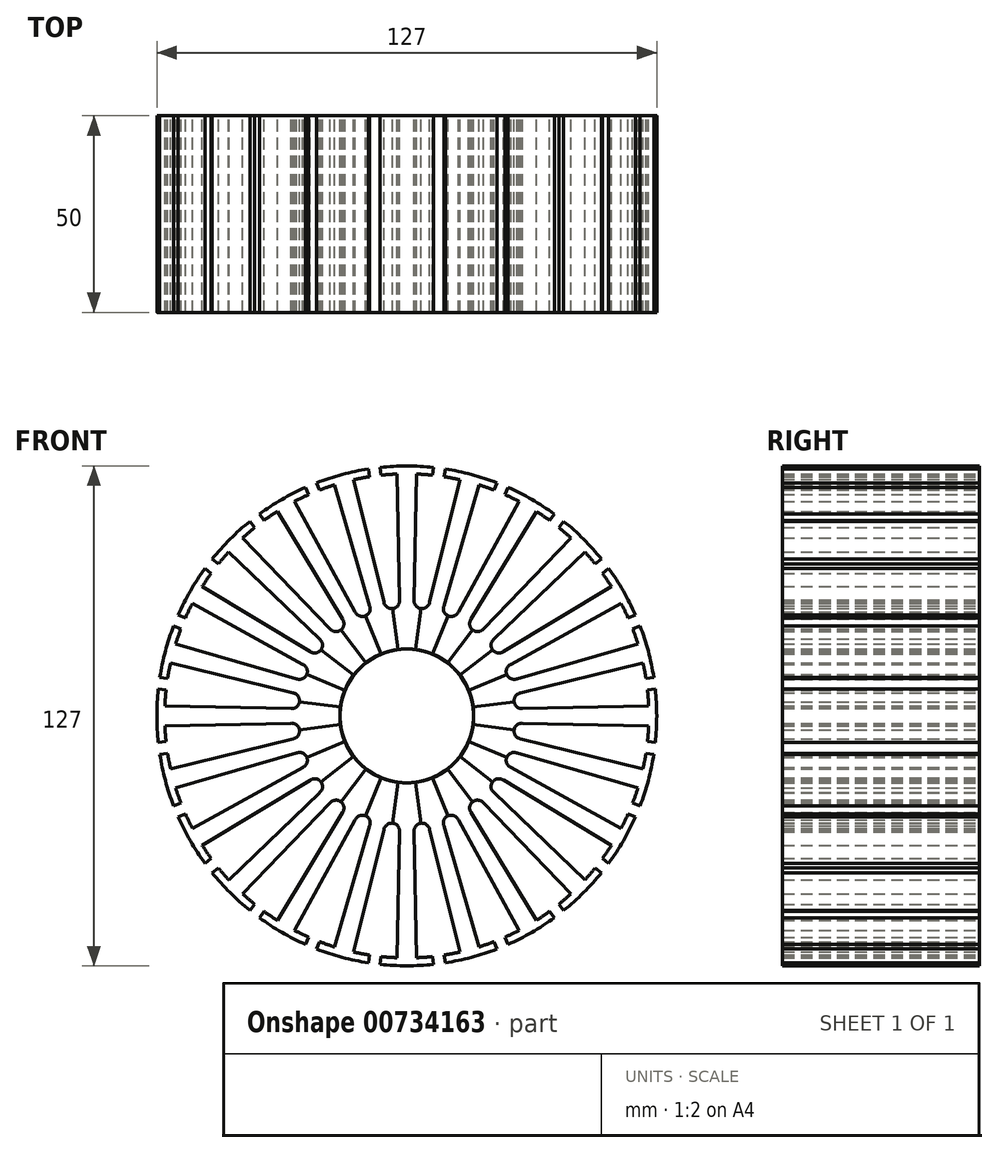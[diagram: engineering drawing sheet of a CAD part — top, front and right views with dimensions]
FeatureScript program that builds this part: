
annotation { "Feature Type Name" : "Feature", "Feature Type Description" : "" }
export const myFeature = defineFeature(function(context is Context, id is Id, definition is map)
    precondition{}
    {
        {
            var Q0;
            Q0=qCreatedBy(makeId("Front.planeOp"),FACE);
            var sketch = newSketch(context, id + "F0", { "sketchPlane" : qUnion([Q0])});
            skCircle(sketch, "E0", {"center": v(0, 0) * mm, "radius": 17 * mm});
            skArc(sketch, "E1", {"start": v(-9.51, 60.76) * mm, "mid": v(-11.5, 60.41) * mm, "end": v(-13.48, 60) * mm});
            skArc(sketch, "E2", {"start": v(1.86, 29.44) * mm, "mid": v(2.28, 28) * mm, "end": v(3.59, 27.26) * mm});
            skArc(sketch, "E3.MirrorC", {"start": v(-1.86, 29.44) * mm, "mid": v(-2.28, 28) * mm, "end": v(-3.59, 27.26) * mm});
            skArc(sketch, "E4.MirrorC", {"start": v(13.1, 26.43) * mm, "mid": v(10.52, 25.4) * mm, "end": v(9.42, 27.96) * mm});
            skArc(sketch, "E5.MirrorC", {"start": v(16.33, 24.57) * mm, "mid": v(16.74, 21.82) * mm, "end": v(19.5, 22.13) * mm});
            skArc(sketch, "E6.MirrorC", {"start": v(24.57, 16.33) * mm, "mid": v(23.1, 15.98) * mm, "end": v(21.82, 16.74) * mm});
            skArc(sketch, "E7.MirrorC", {"start": v(26.43, 13.1) * mm, "mid": v(25.4, 10.52) * mm, "end": v(27.96, 9.42) * mm});
            skArc(sketch, "E8.MirrorC", {"start": v(29.44, 1.86) * mm, "mid": v(27.26, 3.59) * mm, "end": v(28.92, 5.82) * mm});
            skArc(sketch, "E9.MirrorC", {"start": v(29.44, -1.86) * mm, "mid": v(27.26, -3.59) * mm, "end": v(28.92, -5.82) * mm});
            skArc(sketch, "E10.MirrorC", {"start": v(26.43, -13.1) * mm, "mid": v(25.4, -10.52) * mm, "end": v(27.96, -9.42) * mm});
            skArc(sketch, "E11.MirrorC", {"start": v(24.57, -16.33) * mm, "mid": v(21.82, -16.74) * mm, "end": v(22.13, -19.5) * mm});
            skArc(sketch, "E12.MirrorC", {"start": v(16.33, -24.57) * mm, "mid": v(16.74, -21.82) * mm, "end": v(19.5, -22.13) * mm});
            skArc(sketch, "E13.MirrorC", {"start": v(13.1, -26.43) * mm, "mid": v(10.52, -25.4) * mm, "end": v(9.42, -27.96) * mm});
            skArc(sketch, "E14.MirrorC", {"start": v(1.86, -29.44) * mm, "mid": v(3.59, -27.26) * mm, "end": v(5.82, -28.92) * mm});
            skArc(sketch, "E15.MirrorC", {"start": v(-1.86, -29.44) * mm, "mid": v(-3.59, -27.26) * mm, "end": v(-5.82, -28.92) * mm});
            skArc(sketch, "E16.MirrorC", {"start": v(-13.1, -26.43) * mm, "mid": v(-10.52, -25.4) * mm, "end": v(-9.42, -27.96) * mm});
            skArc(sketch, "E17.MirrorC", {"start": v(-16.33, -24.57) * mm, "mid": v(-16.74, -21.82) * mm, "end": v(-19.5, -22.13) * mm});
            skArc(sketch, "E18.MirrorC", {"start": v(-24.57, -16.33) * mm, "mid": v(-21.82, -16.74) * mm, "end": v(-22.13, -19.5) * mm});
            skArc(sketch, "E19.MirrorC", {"start": v(-26.43, -13.1) * mm, "mid": v(-25.4, -10.52) * mm, "end": v(-27.96, -9.42) * mm});
            skArc(sketch, "E20.MirrorC", {"start": v(-29.44, -1.86) * mm, "mid": v(-27.26, -3.59) * mm, "end": v(-28.92, -5.82) * mm});
            skArc(sketch, "E21.MirrorC", {"start": v(-29.44, 1.86) * mm, "mid": v(-27.26, 3.59) * mm, "end": v(-28.92, 5.82) * mm});
            skArc(sketch, "E22.MirrorC", {"start": v(-26.43, 13.1) * mm, "mid": v(-25.4, 10.52) * mm, "end": v(-27.96, 9.42) * mm});
            skArc(sketch, "E23.MirrorC", {"start": v(-24.57, 16.33) * mm, "mid": v(-21.82, 16.74) * mm, "end": v(-22.13, 19.5) * mm});
            skArc(sketch, "E24.MirrorC", {"start": v(-13.1, 26.43) * mm, "mid": v(-10.52, 25.4) * mm, "end": v(-9.42, 27.96) * mm});
            skArc(sketch, "E25.MirrorC", {"start": v(-16.33, 24.57) * mm, "mid": v(-16.74, 21.82) * mm, "end": v(-19.5, 22.13) * mm});
            skLineSegment(sketch, "E26", {"start": v(-2.5, 61.45) * mm, "end": v(-1.86, 29.44) * mm});
            skLineSegment(sketch, "E27", {"start": v(2.5, 61.45) * mm, "end": v(1.85, 29.44) * mm});
            skLineSegment(sketch, "E28.MirrorCS", {"start": v(13.49, 60) * mm, "end": v(5.83, 28.92) * mm});
            skLineSegment(sketch, "E29.MirrorCS", {"start": v(-13.48, 60) * mm, "end": v(-5.82, 28.92) * mm});
            skLineSegment(sketch, "E30.MirrorCS", {"start": v(18.32, 58.7) * mm, "end": v(9.41, 27.96) * mm});
            skLineSegment(sketch, "E31.MirrorCS", {"start": v(28.56, 54.47) * mm, "end": v(13.12, 26.42) * mm});
            skLineSegment(sketch, "E32.MirrorCS", {"start": v(32.9, 51.96) * mm, "end": v(16.33, 24.57) * mm});
            skLineSegment(sketch, "E33.MirrorCS", {"start": v(41.68, 45.22) * mm, "end": v(19.5, 22.13) * mm});
            skLineSegment(sketch, "E34.MirrorCS", {"start": v(45.22, 41.68) * mm, "end": v(22.13, 19.5) * mm});
            skLineSegment(sketch, "E35.MirrorCS", {"start": v(54.47, 28.56) * mm, "end": v(26.42, 13.12) * mm});
            skLineSegment(sketch, "E36.MirrorCS", {"start": v(58.7, 18.32) * mm, "end": v(27.96, 9.41) * mm});
            skLineSegment(sketch, "E37.MirrorCS", {"start": v(60, 13.49) * mm, "end": v(28.92, 5.83) * mm});
            skLineSegment(sketch, "E38.MirrorCS", {"start": v(61.45, 2.5) * mm, "end": v(29.44, 1.85) * mm});
            skLineSegment(sketch, "E39.MirrorCS", {"start": v(61.45, -2.5) * mm, "end": v(29.44, -1.86) * mm});
            skLineSegment(sketch, "E40.MirrorCS", {"start": v(60, -13.48) * mm, "end": v(28.92, -5.82) * mm});
            skLineSegment(sketch, "E41.MirrorCS", {"start": v(58.7, -18.33) * mm, "end": v(27.96, -9.42) * mm});
            skLineSegment(sketch, "E42.MirrorCS", {"start": v(54.47, -28.55) * mm, "end": v(26.43, -13.1) * mm});
            skLineSegment(sketch, "E43.MirrorCS", {"start": v(51.97, -32.89) * mm, "end": v(24.57, -16.33) * mm});
            skLineSegment(sketch, "E44.MirrorCS", {"start": v(45.22, -41.68) * mm, "end": v(22.13, -19.5) * mm});
            skLineSegment(sketch, "E45.MirrorCS", {"start": v(41.68, -45.22) * mm, "end": v(19.5, -22.13) * mm});
            skLineSegment(sketch, "E46.MirrorCS", {"start": v(32.89, -51.97) * mm, "end": v(16.33, -24.57) * mm});
            skLineSegment(sketch, "E47.MirrorCS", {"start": v(51.96, 32.9) * mm, "end": v(24.57, 16.33) * mm});
            skLineSegment(sketch, "E48.MirrorCS", {"start": v(28.56, -54.47) * mm, "end": v(13.12, -26.42) * mm});
            skLineSegment(sketch, "E49.MirrorCS", {"start": v(18.32, -58.7) * mm, "end": v(9.41, -27.96) * mm});
            skLineSegment(sketch, "E50.MirrorCS", {"start": v(13.49, -60) * mm, "end": v(5.83, -28.92) * mm});
            skLineSegment(sketch, "E51.MirrorCS", {"start": v(2.5, -61.45) * mm, "end": v(1.85, -29.44) * mm});
            skLineSegment(sketch, "E52.MirrorCS", {"start": v(-2.5, -61.45) * mm, "end": v(-1.85, -29.44) * mm});
            skLineSegment(sketch, "E53.MirrorCS", {"start": v(-13.49, -60) * mm, "end": v(-5.83, -28.92) * mm});
            skLineSegment(sketch, "E54.MirrorCS", {"start": v(-18.32, -58.7) * mm, "end": v(-9.41, -27.96) * mm});
            skLineSegment(sketch, "E55.MirrorCS", {"start": v(-28.56, -54.47) * mm, "end": v(-13.12, -26.42) * mm});
            skLineSegment(sketch, "E56.MirrorCS", {"start": v(-32.89, -51.97) * mm, "end": v(-16.33, -24.57) * mm});
            skLineSegment(sketch, "E57.MirrorCS", {"start": v(-41.68, -45.22) * mm, "end": v(-19.5, -22.13) * mm});
            skLineSegment(sketch, "E58.MirrorCS", {"start": v(-45.22, -41.68) * mm, "end": v(-22.13, -19.5) * mm});
            skLineSegment(sketch, "E59.MirrorCS", {"start": v(-51.97, -32.89) * mm, "end": v(-24.57, -16.33) * mm});
            skLineSegment(sketch, "E60.MirrorCS", {"start": v(-54.47, -28.56) * mm, "end": v(-26.42, -13.12) * mm});
            skLineSegment(sketch, "E61.MirrorCS", {"start": v(-58.7, -18.32) * mm, "end": v(-27.96, -9.41) * mm});
            skLineSegment(sketch, "E62.MirrorCS", {"start": v(-60, -13.49) * mm, "end": v(-28.92, -5.83) * mm});
            skLineSegment(sketch, "E63.MirrorCS", {"start": v(-61.45, -2.5) * mm, "end": v(-29.44, -1.85) * mm});
            skLineSegment(sketch, "E64.MirrorCS", {"start": v(-61.45, 2.5) * mm, "end": v(-29.44, 1.85) * mm});
            skLineSegment(sketch, "E65.MirrorCS", {"start": v(-60, 13.49) * mm, "end": v(-28.92, 5.83) * mm});
            skLineSegment(sketch, "E66.MirrorCS", {"start": v(-58.7, 18.32) * mm, "end": v(-27.96, 9.41) * mm});
            skLineSegment(sketch, "E67.MirrorCS", {"start": v(-54.47, 28.56) * mm, "end": v(-26.42, 13.12) * mm});
            skLineSegment(sketch, "E68.MirrorCS", {"start": v(-51.97, 32.89) * mm, "end": v(-24.57, 16.33) * mm});
            skLineSegment(sketch, "E69.MirrorCS", {"start": v(-45.22, 41.68) * mm, "end": v(-22.13, 19.5) * mm});
            skLineSegment(sketch, "E70.MirrorCS", {"start": v(-41.68, 45.22) * mm, "end": v(-19.5, 22.13) * mm});
            skLineSegment(sketch, "E71.MirrorCS", {"start": v(-32.89, 51.97) * mm, "end": v(-16.33, 24.57) * mm});
            skLineSegment(sketch, "E72.MirrorCS", {"start": v(-28.56, 54.47) * mm, "end": v(-13.12, 26.42) * mm});
            skLineSegment(sketch, "E73.MirrorCS", {"start": v(-18.32, 58.7) * mm, "end": v(-9.41, 27.96) * mm});
            skArc(sketch, "E74.MirrorCS", {"start": v(22.13, 19.5) * mm, "mid": v(21.42, 18.19) * mm, "end": v(21.82, 16.74) * mm});
            skLineSegment(sketch, "E75.MirrorCS", {"start": v(-6.8, 63.13) * mm, "end": v(-6.54, 61.15) * mm});
            skLineSegment(sketch, "E76.MirrorCS", {"start": v(-9.77, 62.74) * mm, "end": v(-9.51, 60.76) * mm});
            skLineSegment(sketch, "E77.MirrorCS", {"start": v(-22.9, 59.22) * mm, "end": v(-22.14, 57.38) * mm});
            skLineSegment(sketch, "E78.MirrorCS", {"start": v(-25.69, 58.1) * mm, "end": v(-24.91, 56.23) * mm});
            skLineSegment(sketch, "E79.MirrorCS", {"start": v(-37.47, 51.3) * mm, "end": v(-36.24, 49.69) * mm});
            skLineSegment(sketch, "E80.MirrorCS", {"start": v(-39.84, 49.45) * mm, "end": v(-38.62, 47.86) * mm});
            skLineSegment(sketch, "E81.MirrorCS", {"start": v(-49.45, 39.84) * mm, "end": v(-47.86, 38.62) * mm});
            skLineSegment(sketch, "E82.MirrorCS", {"start": v(-51.3, 37.47) * mm, "end": v(-49.69, 36.24) * mm});
            skLineSegment(sketch, "E83.MirrorCS", {"start": v(-59.22, 22.9) * mm, "end": v(-57.38, 22.14) * mm});
            skLineSegment(sketch, "E84.MirrorCS", {"start": v(-58.1, 25.69) * mm, "end": v(-56.23, 24.91) * mm});
            skLineSegment(sketch, "E85.MirrorCS", {"start": v(-62.74, 9.77) * mm, "end": v(-60.76, 9.51) * mm});
            skLineSegment(sketch, "E86.MirrorCS", {"start": v(-63.15, 6.8) * mm, "end": v(-61.15, 6.54) * mm});
            skLineSegment(sketch, "E87.MirrorCS", {"start": v(-63.15, -6.8) * mm, "end": v(-61.15, -6.54) * mm});
            skLineSegment(sketch, "E88.MirrorCS", {"start": v(-62.74, -9.77) * mm, "end": v(-60.76, -9.51) * mm});
            skLineSegment(sketch, "E89.MirrorCS", {"start": v(-59.22, -22.9) * mm, "end": v(-57.38, -22.14) * mm});
            skLineSegment(sketch, "E90.MirrorCS", {"start": v(-58.1, -25.69) * mm, "end": v(-56.23, -24.91) * mm});
            skLineSegment(sketch, "E91.MirrorCS", {"start": v(-51.3, -37.47) * mm, "end": v(-49.69, -36.24) * mm});
            skLineSegment(sketch, "E92.MirrorCS", {"start": v(-49.45, -39.84) * mm, "end": v(-47.86, -38.62) * mm});
            skLineSegment(sketch, "E93.MirrorCS", {"start": v(-39.84, -49.45) * mm, "end": v(-38.62, -47.86) * mm});
            skLineSegment(sketch, "E94.MirrorCS", {"start": v(-37.47, -51.3) * mm, "end": v(-36.24, -49.69) * mm});
            skLineSegment(sketch, "E95.MirrorCS", {"start": v(-25.69, -58.1) * mm, "end": v(-24.91, -56.23) * mm});
            skLineSegment(sketch, "E96.MirrorCS", {"start": v(-22.9, -59.22) * mm, "end": v(-22.14, -57.38) * mm});
            skLineSegment(sketch, "E97.MirrorCS", {"start": v(-9.77, -62.74) * mm, "end": v(-9.51, -60.76) * mm});
            skLineSegment(sketch, "E98.MirrorCS", {"start": v(-6.8, -63.15) * mm, "end": v(-6.54, -61.15) * mm});
            skLineSegment(sketch, "E99.MirrorCS", {"start": v(6.8, -63.15) * mm, "end": v(6.54, -61.15) * mm});
            skLineSegment(sketch, "E100.MirrorCS", {"start": v(9.77, -62.74) * mm, "end": v(9.51, -60.76) * mm});
            skLineSegment(sketch, "E101.MirrorCS", {"start": v(22.9, -59.22) * mm, "end": v(22.14, -57.38) * mm});
            skLineSegment(sketch, "E102.MirrorCS", {"start": v(25.69, -58.1) * mm, "end": v(24.91, -56.23) * mm});
            skLineSegment(sketch, "E103.MirrorCS", {"start": v(37.47, -51.3) * mm, "end": v(36.24, -49.69) * mm});
            skLineSegment(sketch, "E104.MirrorCS", {"start": v(39.84, -49.45) * mm, "end": v(38.62, -47.86) * mm});
            skLineSegment(sketch, "E105.MirrorCS", {"start": v(49.45, -39.84) * mm, "end": v(47.86, -38.62) * mm});
            skLineSegment(sketch, "E106.MirrorCS", {"start": v(51.3, -37.47) * mm, "end": v(49.69, -36.24) * mm});
            skLineSegment(sketch, "E107.MirrorCS", {"start": v(58.1, -25.69) * mm, "end": v(56.23, -24.91) * mm});
            skLineSegment(sketch, "E108.MirrorCS", {"start": v(59.22, -22.9) * mm, "end": v(57.38, -22.14) * mm});
            skLineSegment(sketch, "E109.MirrorCS", {"start": v(63.15, -6.8) * mm, "end": v(61.15, -6.54) * mm});
            skLineSegment(sketch, "E110.MirrorCS", {"start": v(62.74, -9.77) * mm, "end": v(60.76, -9.51) * mm});
            skLineSegment(sketch, "E111.MirrorCS", {"start": v(63.15, 6.8) * mm, "end": v(61.15, 6.54) * mm});
            skLineSegment(sketch, "E112.MirrorCS", {"start": v(62.74, 9.77) * mm, "end": v(60.76, 9.51) * mm});
            skLineSegment(sketch, "E113.MirrorCS", {"start": v(59.22, 22.9) * mm, "end": v(57.38, 22.14) * mm});
            skLineSegment(sketch, "E114.MirrorCS", {"start": v(58.1, 25.69) * mm, "end": v(56.23, 24.91) * mm});
            skLineSegment(sketch, "E115.MirrorCS", {"start": v(51.3, 37.47) * mm, "end": v(49.69, 36.24) * mm});
            skLineSegment(sketch, "E116.MirrorCS", {"start": v(49.45, 39.84) * mm, "end": v(47.86, 38.62) * mm});
            skLineSegment(sketch, "E117.MirrorCS", {"start": v(39.84, 49.45) * mm, "end": v(38.62, 47.86) * mm});
            skLineSegment(sketch, "E118.MirrorCS", {"start": v(37.47, 51.3) * mm, "end": v(36.24, 49.69) * mm});
            skLineSegment(sketch, "E119.MirrorCS", {"start": v(6.8, 63.13) * mm, "end": v(6.54, 61.15) * mm});
            skLineSegment(sketch, "E120.MirrorCS", {"start": v(9.77, 62.74) * mm, "end": v(9.51, 60.76) * mm});
            skLineSegment(sketch, "E121.MirrorCS", {"start": v(22.9, 59.22) * mm, "end": v(22.14, 57.38) * mm});
            skLineSegment(sketch, "E122.MirrorCS", {"start": v(25.69, 58.1) * mm, "end": v(24.91, 56.23) * mm});
            skArc(sketch, "E123.trimOffspring", {"start": v(-24.91, 56.23) * mm, "mid": v(-26.75, 55.38) * mm, "end": v(-28.56, 54.47) * mm});
            skArc(sketch, "E124.trimOffspring", {"start": v(-25.68, 58.08) * mm, "mid": v(-31.75, 55) * mm, "end": v(-37.46, 51.28) * mm});
            skArc(sketch, "E125.trimOffspring", {"start": v(-38.62, 47.86) * mm, "mid": v(-40.17, 46.57) * mm, "end": v(-41.68, 45.22) * mm});
            skArc(sketch, "E126.trimOffspring", {"start": v(-39.84, 49.45) * mm, "mid": v(-44.9, 44.9) * mm, "end": v(-49.45, 39.84) * mm});
            skArc(sketch, "E127.trimOffspring", {"start": v(-57.38, 22.14) * mm, "mid": v(-58.07, 20.24) * mm, "end": v(-58.7, 18.32) * mm});
            skArc(sketch, "E128.trimOffspring", {"start": v(-59.22, 22.9) * mm, "mid": v(-61.34, 16.44) * mm, "end": v(-62.74, 9.77) * mm});
            skArc(sketch, "E129.trimOffspring", {"start": v(-51.28, 37.46) * mm, "mid": v(-55, 31.75) * mm, "end": v(-58.08, 25.68) * mm});
            skArc(sketch, "E130.trimOffspring", {"start": v(-49.69, 36.24) * mm, "mid": v(-50.86, 34.58) * mm, "end": v(-51.97, 32.89) * mm});
            skArc(sketch, "E131.trimOffspring", {"start": v(-61.15, 6.54) * mm, "mid": v(-61.33, 4.52) * mm, "end": v(-61.45, 2.5) * mm});
            skArc(sketch, "E132.trimOffspring", {"start": v(-63.13, 6.8) * mm, "mid": v(-63.5, 0) * mm, "end": v(-63.13, -6.8) * mm});
            skArc(sketch, "E133.trimOffspring", {"start": v(-60.76, -9.51) * mm, "mid": v(-60.41, -11.5) * mm, "end": v(-60, -13.49) * mm});
            skArc(sketch, "E134.trimOffspring", {"start": v(-56.23, -24.91) * mm, "mid": v(-55.38, -26.75) * mm, "end": v(-54.47, -28.56) * mm});
            skArc(sketch, "E135.trimOffspring", {"start": v(-62.74, -9.77) * mm, "mid": v(-61.34, -16.44) * mm, "end": v(-59.22, -22.9) * mm});
            skArc(sketch, "E136.trimOffspring", {"start": v(-58.08, -25.68) * mm, "mid": v(-55, -31.75) * mm, "end": v(-51.28, -37.46) * mm});
            skArc(sketch, "E137.trimOffspring", {"start": v(-49.45, -39.84) * mm, "mid": v(-44.9, -44.9) * mm, "end": v(-39.84, -49.45) * mm});
            skArc(sketch, "E138.trimOffspring", {"start": v(-47.86, -38.62) * mm, "mid": v(-46.57, -40.17) * mm, "end": v(-45.22, -41.68) * mm});
            skArc(sketch, "E139.trimOffspring", {"start": v(-37.46, -51.28) * mm, "mid": v(-31.75, -55) * mm, "end": v(-25.68, -58.08) * mm});
            skArc(sketch, "E140.trimOffspring", {"start": v(-36.24, -49.69) * mm, "mid": v(-34.58, -50.86) * mm, "end": v(-32.89, -51.97) * mm});
            skArc(sketch, "E141.trimOffspring", {"start": v(-22.14, -57.38) * mm, "mid": v(-20.24, -58.07) * mm, "end": v(-18.32, -58.7) * mm});
            skArc(sketch, "E142.trimOffspring", {"start": v(-22.9, -59.22) * mm, "mid": v(-16.44, -61.34) * mm, "end": v(-9.77, -62.74) * mm});
            skArc(sketch, "E143.trimOffspring", {"start": v(-6.54, -61.15) * mm, "mid": v(-4.52, -61.33) * mm, "end": v(-2.5, -61.45) * mm});
            skArc(sketch, "E144.trimOffspring", {"start": v(-6.8, -63.13) * mm, "mid": v(0, -63.5) * mm, "end": v(6.8, -63.13) * mm});
            skArc(sketch, "E145.trimOffspring", {"start": v(9.51, -60.76) * mm, "mid": v(11.5, -60.41) * mm, "end": v(13.49, -60) * mm});
            skArc(sketch, "E146.trimOffspring", {"start": v(9.77, -62.74) * mm, "mid": v(16.44, -61.34) * mm, "end": v(22.9, -59.22) * mm});
            skArc(sketch, "E147.trimOffspring", {"start": v(24.91, -56.23) * mm, "mid": v(26.75, -55.38) * mm, "end": v(28.56, -54.47) * mm});
            skArc(sketch, "E148.trimOffspring", {"start": v(25.68, -58.08) * mm, "mid": v(31.75, -55) * mm, "end": v(37.46, -51.28) * mm});
            skArc(sketch, "E149.trimOffspring", {"start": v(38.62, -47.86) * mm, "mid": v(40.17, -46.57) * mm, "end": v(41.68, -45.22) * mm});
            skArc(sketch, "E150.trimOffspring", {"start": v(39.84, -49.45) * mm, "mid": v(44.9, -44.9) * mm, "end": v(49.45, -39.84) * mm});
            skArc(sketch, "E151.trimOffspring", {"start": v(49.69, -36.24) * mm, "mid": v(50.86, -34.58) * mm, "end": v(51.97, -32.89) * mm});
            skArc(sketch, "E152.trimOffspring", {"start": v(51.28, -37.46) * mm, "mid": v(55, -31.75) * mm, "end": v(58.08, -25.68) * mm});
            skArc(sketch, "E153.trimOffspring", {"start": v(57.38, -22.14) * mm, "mid": v(58.07, -20.24) * mm, "end": v(58.7, -18.33) * mm});
            skArc(sketch, "E154.trimOffspring", {"start": v(59.22, -22.9) * mm, "mid": v(61.34, -16.44) * mm, "end": v(62.74, -9.77) * mm});
            skArc(sketch, "E155.trimOffspring", {"start": v(61.15, -6.54) * mm, "mid": v(61.33, -4.52) * mm, "end": v(61.45, -2.5) * mm});
            skArc(sketch, "E156.trimOffspring", {"start": v(63.13, -6.8) * mm, "mid": v(63.5, 0) * mm, "end": v(63.13, 6.8) * mm});
            skArc(sketch, "E157.trimOffspring", {"start": v(60.76, 9.51) * mm, "mid": v(60.41, 11.5) * mm, "end": v(60, 13.49) * mm});
            skArc(sketch, "E158.trimOffspring", {"start": v(56.23, 24.91) * mm, "mid": v(55.38, 26.75) * mm, "end": v(54.47, 28.56) * mm});
            skArc(sketch, "E159.trimOffspring", {"start": v(58.08, 25.68) * mm, "mid": v(55, 31.75) * mm, "end": v(51.28, 37.46) * mm});
            skArc(sketch, "E160.trimOffspring", {"start": v(47.86, 38.62) * mm, "mid": v(46.57, 40.17) * mm, "end": v(45.22, 41.68) * mm});
            skArc(sketch, "E161.trimOffspring", {"start": v(49.45, 39.84) * mm, "mid": v(44.9, 44.9) * mm, "end": v(39.84, 49.45) * mm});
            skArc(sketch, "E162.trimOffspring", {"start": v(36.24, 49.69) * mm, "mid": v(34.59, 50.85) * mm, "end": v(32.9, 51.96) * mm});
            skArc(sketch, "E163.trimOffspring", {"start": v(37.46, 51.28) * mm, "mid": v(31.75, 55) * mm, "end": v(25.68, 58.08) * mm});
            skArc(sketch, "E164.trimOffspring", {"start": v(22.14, 57.38) * mm, "mid": v(20.24, 58.07) * mm, "end": v(18.32, 58.7) * mm});
            skArc(sketch, "E165.trimOffspring", {"start": v(22.9, 59.22) * mm, "mid": v(16.44, 61.34) * mm, "end": v(9.77, 62.74) * mm});
            skArc(sketch, "E166.trimOffspring", {"start": v(6.8, 63.13) * mm, "mid": v(0, 63.5) * mm, "end": v(-6.8, 63.13) * mm});
            skArc(sketch, "E167.trimOffspring", {"start": v(6.54, 61.15) * mm, "mid": v(4.52, 61.33) * mm, "end": v(2.5, 61.45) * mm});
            skArc(sketch, "E168", {"start": v(-22.9, 59.22) * mm, "mid": v(-16.44, 61.34) * mm, "end": v(-9.77, 62.74) * mm});
            skArc(sketch, "E169.trimOffspring", {"start": v(-45.22, 41.68) * mm, "mid": v(-46.57, 40.17) * mm, "end": v(-47.86, 38.62) * mm});
            skArc(sketch, "E170.trimOffspring", {"start": v(-32.89, 51.97) * mm, "mid": v(-34.58, 50.86) * mm, "end": v(-36.24, 49.69) * mm});
            skArc(sketch, "E171.trimOffspring", {"start": v(-54.47, 28.56) * mm, "mid": v(-55.38, 26.75) * mm, "end": v(-56.23, 24.91) * mm});
            skArc(sketch, "E172.trimOffspring", {"start": v(-60, 13.49) * mm, "mid": v(-60.41, 11.5) * mm, "end": v(-60.76, 9.51) * mm});
            skArc(sketch, "E173.trimOffspring", {"start": v(-58.7, -18.32) * mm, "mid": v(-58.07, -20.24) * mm, "end": v(-57.38, -22.14) * mm});
            skArc(sketch, "E174.trimOffspring", {"start": v(-51.97, -32.89) * mm, "mid": v(-50.86, -34.58) * mm, "end": v(-49.69, -36.24) * mm});
            skArc(sketch, "E175.trimOffspring", {"start": v(-61.45, -2.5) * mm, "mid": v(-61.33, -4.52) * mm, "end": v(-61.15, -6.54) * mm});
            skArc(sketch, "E176.trimOffspring", {"start": v(-41.68, -45.22) * mm, "mid": v(-40.17, -46.57) * mm, "end": v(-38.62, -47.86) * mm});
            skArc(sketch, "E177.trimOffspring", {"start": v(-28.56, -54.47) * mm, "mid": v(-26.75, -55.38) * mm, "end": v(-24.91, -56.23) * mm});
            skArc(sketch, "E178.trimOffspring", {"start": v(-13.49, -60) * mm, "mid": v(-11.5, -60.41) * mm, "end": v(-9.51, -60.76) * mm});
            skArc(sketch, "E179.trimOffspring", {"start": v(2.5, -61.45) * mm, "mid": v(4.52, -61.33) * mm, "end": v(6.54, -61.15) * mm});
            skArc(sketch, "E180.trimOffspring", {"start": v(18.32, -58.7) * mm, "mid": v(20.24, -58.07) * mm, "end": v(22.14, -57.38) * mm});
            skArc(sketch, "E181.trimOffspring", {"start": v(32.89, -51.97) * mm, "mid": v(34.58, -50.86) * mm, "end": v(36.24, -49.69) * mm});
            skArc(sketch, "E182.trimOffspring", {"start": v(45.22, -41.68) * mm, "mid": v(46.57, -40.17) * mm, "end": v(47.86, -38.62) * mm});
            skArc(sketch, "E183.trimOffspring", {"start": v(54.47, -28.55) * mm, "mid": v(55.38, -26.75) * mm, "end": v(56.23, -24.91) * mm});
            skArc(sketch, "E184.trimOffspring", {"start": v(60, -13.48) * mm, "mid": v(60.41, -11.5) * mm, "end": v(60.76, -9.51) * mm});
            skArc(sketch, "E185.trimOffspring", {"start": v(61.45, 2.5) * mm, "mid": v(61.33, 4.52) * mm, "end": v(61.15, 6.54) * mm});
            skArc(sketch, "E186.trimOffspring", {"start": v(58.7, 18.32) * mm, "mid": v(58.07, 20.24) * mm, "end": v(57.38, 22.14) * mm});
            skArc(sketch, "E187.trimOffspring", {"start": v(51.96, 32.9) * mm, "mid": v(50.85, 34.59) * mm, "end": v(49.69, 36.24) * mm});
            skArc(sketch, "E188.trimOffspring", {"start": v(41.68, 45.22) * mm, "mid": v(40.17, 46.57) * mm, "end": v(38.62, 47.86) * mm});
            skArc(sketch, "E189.trimOffspring", {"start": v(28.56, 54.47) * mm, "mid": v(26.75, 55.38) * mm, "end": v(24.91, 56.23) * mm});
            skArc(sketch, "E190.trimOffspring", {"start": v(13.49, 60) * mm, "mid": v(11.5, 60.41) * mm, "end": v(9.51, 60.76) * mm});
            skArc(sketch, "E191.trimOffspring", {"start": v(-2.5, 61.45) * mm, "mid": v(-4.52, 61.33) * mm, "end": v(-6.54, 61.15) * mm});
            skArc(sketch, "E192.trimOffspring", {"start": v(-18.32, 58.7) * mm, "mid": v(-20.24, 58.07) * mm, "end": v(-22.14, 57.38) * mm});
            skArc(sketch, "E193", {"start": v(59.22, 22.9) * mm, "mid": v(61.34, 16.44) * mm, "end": v(62.74, 9.77) * mm});
            skLineSegment(sketch, "E194", {"start": v(3.59, 27.26) * mm, "end": v(0, 0) * mm});
            skLineSegment(sketch, "E195", {"start": v(-3.59, 27.26) * mm, "end": v(0, 0) * mm});
            skLineSegment(sketch, "E196", {"start": v(1.85, 29.44) * mm, "end": v(1.86, 29.44) * mm});
            skSolve(sketch);
        }
        {
            var Q0;
            Q0 = qSketchRegion(id + "F0", true);
            extrude(context, id + "F1", {"entities" : qUnion([Q0]), "depth" : 50 * mm, "offsetDistance" : 25 * mm});
        }
        {
            var Q0;
            Q0=makeQuery(id+"F1.opExtrude","SWEPT_BODY",BODY,{"disambiguationData":[OSD([sQuery(id+"F0.wireOp",EDGE,"E0"),sQuery(id+"F0.wireOp",EDGE,"E2"),sQuery(id+"F0.wireOp",EDGE,"E3.MirrorC"),sQuery(id+"F0.wireOp",EDGE,"E26"),sQuery(id+"F0.wireOp",EDGE,"E27"),sQuery(id+"F0.wireOp",EDGE,"E75.MirrorCS"),sQuery(id+"F0.wireOp",EDGE,"E119.MirrorCS"),sQuery(id+"F0.wireOp",EDGE,"E166.trimOffspring"),sQuery(id+"F0.wireOp",EDGE,"E167.trimOffspring"),sQuery(id+"F0.wireOp",EDGE,"E191.trimOffspring"),sQuery(id+"F0.wireOp",EDGE,"E194"),sQuery(id+"F0.wireOp",EDGE,"E195"),sQuery(id+"F0.wireOp",EDGE,"E196")])]});
            var Q1;
            Q1=makeQuery(id+"F1.opExtrude","SWEPT_FACE",FACE,{"disambiguationData":[OSD([sQuery(id+"F0.wireOp",EDGE,"E0")])]});
            circularPattern(context, id + "F2", {"entities" : qUnion([Q0]), "axis" : qUnion([Q1]), "angle" : 360 * degree, "instanceCount" : 24, "equalSpace" : true});
        }
    });
